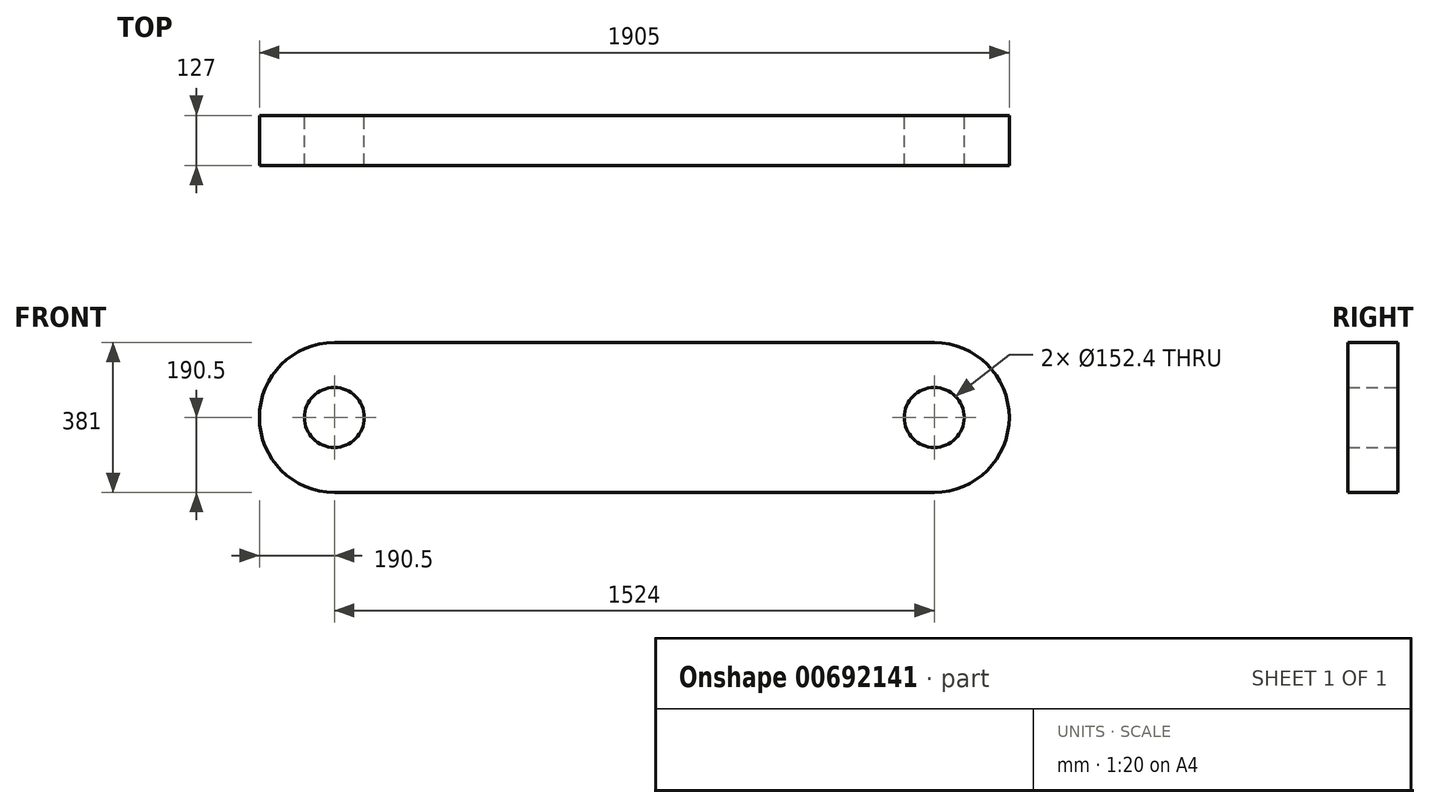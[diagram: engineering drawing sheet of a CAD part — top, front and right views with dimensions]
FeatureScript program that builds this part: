
annotation { "Feature Type Name" : "Feature", "Feature Type Description" : "" }
export const myFeature = defineFeature(function(context is Context, id is Id, definition is map)
    precondition{}
    {
        {
            var Q0;
            Q0=qCreatedBy(makeId("Front.planeOp"),FACE);
            var sketch = newSketch(context, id + "F0", { "sketchPlane" : qUnion([Q0])});
            skLineSegment(sketch, "E0.bottom", {"start": v(-762, 190.5) * mm, "end": v(762, 190.5) * mm});
            skLineSegment(sketch, "E0.top", {"start": v(-762, -190.5) * mm, "end": v(762, -190.5) * mm});
            skLineSegment(sketch, "E0.left", {"start": v(-762, 190.5) * mm, "end": v(-762, -190.5) * mm, "construction": true});
            skLineSegment(sketch, "E0.right", {"start": v(762, 190.5) * mm, "end": v(762, -190.5) * mm, "construction": true});
            skArc(sketch, "E1", {"start": v(-762, 190.5) * mm, "mid": v(-952.5, 0) * mm, "end": v(-762, -190.5) * mm});
            skArc(sketch, "E2.MirrorCS", {"start": v(762, 190.5) * mm, "mid": v(952.5, 0) * mm, "end": v(762, -190.5) * mm});
            skCircle(sketch, "E3", {"center": v(-762, 0) * mm, "radius": 76.2 * mm});
            skCircle(sketch, "E4", {"center": v(762, 0) * mm, "radius": 76.2 * mm});
            skSolve(sketch);
        }
        {
            var Q0;
            Q0=qSketchRegion(id+"F0",true);
            extrude(context, id + "F1", {"entities" : qUnion([Q0]), "depth" : 127 * mm, "offsetDistance" : 25.4 * mm});
        }
    });
